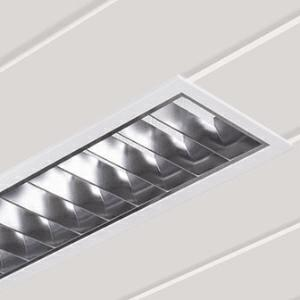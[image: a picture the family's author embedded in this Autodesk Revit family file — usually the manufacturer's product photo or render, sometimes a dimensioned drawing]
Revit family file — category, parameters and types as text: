
# Revit family: 3f_filippi_-_l_560_2s_3f_filippi_-_270939_-_l_562x24w_led_2s_221x1256
name_source: partatom
category: Lighting Fixtures
units: mm (PartAtom-declared; Revit-internal decimal feet)

## family parameters
Cut with Voids When Loaded = No
Host = Face
Light Source = No
Part Type = Normal
Room Calculation Point = No
Round Connector Dimension = Use Diameter
Shared = No

## types (1)
- 3F Filippi - L 560 2S (1 x LED, 5547 lm, 54 W, 4000 K)
    Apparent Load = 54 VA
    Approval mark = ENEC
    CIE Flux Codes = 77 98 100 100 100
    Color Rendering = 80
    Color Temperature = 4000 K
    Control Gear = Electronic ballast
    Default Elevation = 1800 mm
    Description = ILLUMINOTECHNICAL
Luminous efficiency 100% (DLOR 100%, ULOR 0%).
Initial luminous flux of the luminaire 5547 lm.
Direct symmetric distribution.
Installation Interdistance Transv.D = 0.95 x hu - Long.D = 1.08 x hu.
Average luminance <1500 cd/m² for radial angles >65°.
Tabular UGR (CIE 117 - 4H-8H; S=0.25H; 70/50/20): RUG 15.3 - 17.7.
Beam angle: 62° - 78°.
Luminous efficacy 103 lm/W.
Lifetime (L93/B10): 30000 h. (tq+25°C)
Lifetime (L90/B10): 50000 h. (tq+25°C)
Lifetime (L85/B10): 80000 h. (tq+25°C)
Lifetime (L80/B10): 100000 h. (tq+25°C)
Sudden decreased luminous flux after 50000 hours: 0% (C0).
Photobiological safety in compliance with IEC/TR 62778: RG0 risk exempt, (IEC 62471).
In compliance with IEC/EN 62722-2-1 - IEC/EN 62717 standards.

SOURCE
2 linear LED modules 24W/840.
Energy efficiency class (UE 2019/2020 - UE 2019/2015): D.
CIE 13.3 Colour rendering index: CRI >80 (R9 <50%).
IES TM-30 Fidelity Index: Rf = 84 Rg = 95.
CCT nominal colour temperature 4000 K.
Colour initial tolerance (MacAdam): SDCM 3.

MECHANICAL
Housing in galvannealed steel, painted in white epoxy-polyester.
2S parabolic louvre in semi-specular aluminium, non-reflecting, with transverse blades closed at the top.
Prismatic flat diffuser in transparent methacrylate (PMMA), multilenticular, anti-glare, prismatic exterior, placed above louvre blades.
Film protective against dust and finger marks, adhesive, attached to louvre.
Luminaire with limited surface temperature. - D - (EN 60598-2-24)
Dimensions: 1256x221 mm, height 95 mm. Weight 4.845 kg.
IP20 protection degree.
Mechanical strength to impacts IK02 (0.2 joule).
Glow-wire test resistance 650°C.

ELECTRICAL
Halogen Free electronic wiring 230V-50/60Hz, power factor 0.95, THD <25%, constant output current, SELV, class I, 1 driver.
Power of the luminaire 54 W.
CE - IEC 60598-1 - EN 60598-1.
SAFE FLICKER: PstLM=<1 and SVM=<0.4 (IEC TR 61547-1 and IEC TR 63158), to ensure a more comfortable and safe light.
Luminaire compliant with EN 60598-2-22 for power supply from a centralised emergency system CPSS (Central Power Supply System), not incorporated in the luminaire - high risk areas excluded. The default power and flux are 100% in AC and 100% in DC.
Ambient temperature from 0°C to +25°C.
Temperature class T6 max 85°C.
Relative humidity UR: <85%.

INSTALLATION
Pull-up recessed fitting / Slat ceiling recessed fitting.
False ceiling carving: 190x1230 mm.
All accessories dedicated to this product are available on the Catalog and on our website www.3F-Filippi.com.

APPLICATIONS
In environments with VDTs, managerial offices and staterooms, public offices and schools.

WARNING
Luminaire designed for disposal/recycling at end-of-life.
Replaceable (LED only) light source by a professional. Replaceable control gear by a professional.
    Height = 0 mm  [stored 0 ft]
    Lamp = 1 x LED
    Lamp Light Flux = 5547 lm
    Lamp Power = 54 W
    Lamp count = 1
    Length = 1256 mm
    Lifetime = 50000 h
    Luminous efficacy = 103 lm/W
    Manufacturer = 3F Filippi
    ModVariant = No
    Model = 3F Filippi - 270939 - L 562x24W LED 2S 221x1256
    Mounting Place = Ceiling
    Mounting Type = Recessed
    Number of Poles = 1
    OnlyDefault = Yes
    Power Factor = 1
    Product Name = 3F Filippi - L 560 2S
    Product group = recessed luminaire
    ProductGroupID = 4
    Protection Class = Protection class I
    Protection Degree = IP 20
    RLX_Detail_Level = 1
    RLX_Emergency_Light_Flux = 0 lm
    RLX_Emergency_Type = 0
    RLX_Emergency_Type_DB = No
    RlxData = <blob elided: 60545 chars, md5=c43c0b7e>
    Socket = socket
    Standby Power = 0 W
    System Light Flux = 5547 lm
    System Power = 54 W
    Type Comments = Product without accessories
    Type Image = 3ffilippi_270939.jpg
    URL = http://relux.com
    VarID = ---
    Voltage = 0 V
    Weight = 0.00 kg
    Width = 221 mm

note: [stored X ft] marks values corroborated as IEEE doubles in the binary element streams (Revit-internal decimal feet)

## geometry (parser evidence)
native form markers: Blend x4, Sweep x11
no freeform markers — native parametric forms only
